# Revit family: OHPH
name_source: partatom
category: Mechanical Equipment
units: mm (PartAtom-declared; Revit-internal decimal feet)

## family parameters
Always vertical = Yes
Cut with Voids When Loaded = No
OmniClass Number = 23.40.40.11.17
OmniClass Title = Refrigerated Cases
Part Type = Normal
Room Calculation Point = No
Round Connector Dimension = Use Radius
Shared = No
Work Plane-Based = Yes

## types (14) — shared parameters
16" Shelf = Yes
18" Shelf = Yes
20" Shelf = Yes
BOTTOM ELECTRICAL = Yes
BOTTOM REFRIGERATION PIPING = Yes
Certifications = NSF 7, UL471, CSA
DATE = 04/27/2016
DRAIN PIPING = Yes
Default Elevation = 48"
Defrosts Per Day = 6
Description = High Multi-Deck Merchandiser
Discharge Air Velocity (FPM) = 150 FPM
EQUIPMENT DESCRIPTION = High Multi-Deck Merchandiser
EQUIPMENT MARK = OHPH-NRG-7BF
GLASS = Glass
Height = 76 7/8"
Item Description = High Multi-Deck Merchandiser
LIGHT MATERIAL = GALVANIZED STEEL
Legend Number = OHPH-NRG-7BF
Manufacturer = HILL PHOENIX
Model = OHPH-NRG-7BF
PAINTED METAL UPPER SHELF = PAINTED SHELVES
REAR REFRIGERATION PIPING = Yes
REFRIGERATION PIPING = COPPER PIPE
STAINLESS STEEL = GALVANIZED STEEL
Standard Power Amps = 0 A
Superheat Set Point @ Bulb (°F) = 6-8  °F
TOP ELECTRICAL = Yes
TOP REFRIGERATION PIPING = Yes
TRIM MATERIAL = GALVANIZED STEEL
Timed-Off Defrost Fail-Safe (Min) = 40 (Min)
Timed-Off Defrost Termination Temp = 42 °F
URL = http://www.hillphoenix.com
Width = 43 1/4"

## per-type parameters (varying)
| type | Application Discipline | BTUH Conventional | BTUH Parallel | CENTER LINE | DRAIN LINE | Discharge Air (°F) | Evaporator (°F) | High Efficiency Amps | High Efficiency Watts | High Power (Cornice) Amps | High Power (Cornice) Watts | Length | Length of Cases | Light Length | Lights Per Row | Number of Fans | Refgn | Refgn-2 | Standard Power Watts |
| 04' Cut Produce | Cut Produce | 1263 | 1105 | 24" | 36" | 36 °F | 32 °F | 0 A | 0 W | 0 A | 0 W | 48" | 0" |  | 0 | 0 | 22 1/2" | 7 5/8" | 0 W |
| 06' Cut Produce | Cut Produce | 1263 | 1105 | 36" | 36" | 36 °F | 32 °F | 0 A | 36 W | 0 A | 30 W | 72" | 72" | 3' | 2 | 2 | 28 5/8" | 8 1/2" | 17 W |
| 08' Cut Produce | Cut Produce | 1263 | 1105 | 48" | 48" | 36 °F | 32 °F | 1 A | 54 W | 0 A | 43 W | 96" | 0" | 4' | 2 | 3 | 28 5/8" | 8 1/2" | 24 W |
| 12' Cut Produce | Cut Produce | 1263 | 1105 | 72" | 72" | 36 °F | 32 °F | 1 A | 72 W | 1 A | 65 W | 144" | 0" | 4' | 3 | 4 | 28 5/8" | 8 1/2" | 36 W |
| 04' Bulk Produce | Bulk Produce | 1177 | 1030 | 24" | 36" | 38 °F | 34 °F | 0 A | 0 W | 0 A | 0 W | 48" | 48" |  | 0 | 0 | 22 1/2" | 7 5/8" | 0 W |
| 06' Bulk Produce | Bulk Produce | 1177 | 1030 | 36" | 36" | 38 °F | 34 °F | 0 A | 36 W | 0 A | 30 W | 72" | 72" | 3' | 2 | 2 | 28 5/8" | 8 1/2" | 17 W |
| 08' Bulk Produce | Bulk Produce | 1177 | 1030 | 48" | 48" | 38 °F | 34 °F | 1 A | 54 W | 0 A | 43 W | 96" | 0" | 4' | 2 | 3 | 28 5/8" | 8 1/2" | 24 W |
| 12' Bulk Produce | Bulk Produce | 1177 | 1030 | 72" | 72" | 38 °F | 34 °F | 1 A | 72 W | 1 A | 65 W | 144" | 0" | 4' | 3 | 4 | 28 5/8" | 8 1/2" | 36 W |
| 12' | Cut Produce | 1263 | 1105 | 72" | 72" | 36 °F | 32 °F | 1 A | 71 W | 0 A | 45 W | 144" | 144" | 4' | 3 | 4 | 28 5/8" | 8 1/2" | 18 W |
| 8' | Cut Produce | 1263 | 1105 | 48" | 48" | 36 °F | 32 °F | 1 A | 53 W | 0 A | 30 W | 96" | 96" | 4' | 2 | 3 | 28 5/8" | 8 1/2" | 12 W |
| 6' | Bulk Produce | 1177 | 1030 | 36" | 36" | 38 °F | 34 °F | 0 A | 35 W | 0 A | 24 W | 72" | 72" | 3' | 2 | 2 | 28 5/8" | 8 1/2" | 9 W |
| 4' | Cut Produce | 1263 | 1105 | 24" | 36" | 36 °F | 32 °F | 0 A | 18 W | 0 A | 15 W | 48" | 48" | 4' | 1 | 1 | 22 1/2" | 7 5/8" | 6 W |
| OS 90 WEDGE LEFT | Cut Produce | 1263 | 1105 | 48" | 48" | 36 °F | 32 °F | 1 A | 53 W | 0 A | 30 W | 96" | 96" | 4' | 2 | 3 | 28 5/8" | 8 1/2" | 12 W |
| OS 90 WEDGE RIGHT | Cut Produce | 1263 | 1105 | 48" | 48" | 36 °F | 32 °F | 1 A | 53 W | 0 A | 30 W | 96" | 96" | 4' | 2 | 3 | 28 5/8" | 8 1/2" | 12 W |

## geometry (parser evidence)
native form markers: Blend x17, Sweep x9
no freeform markers — native parametric forms only
